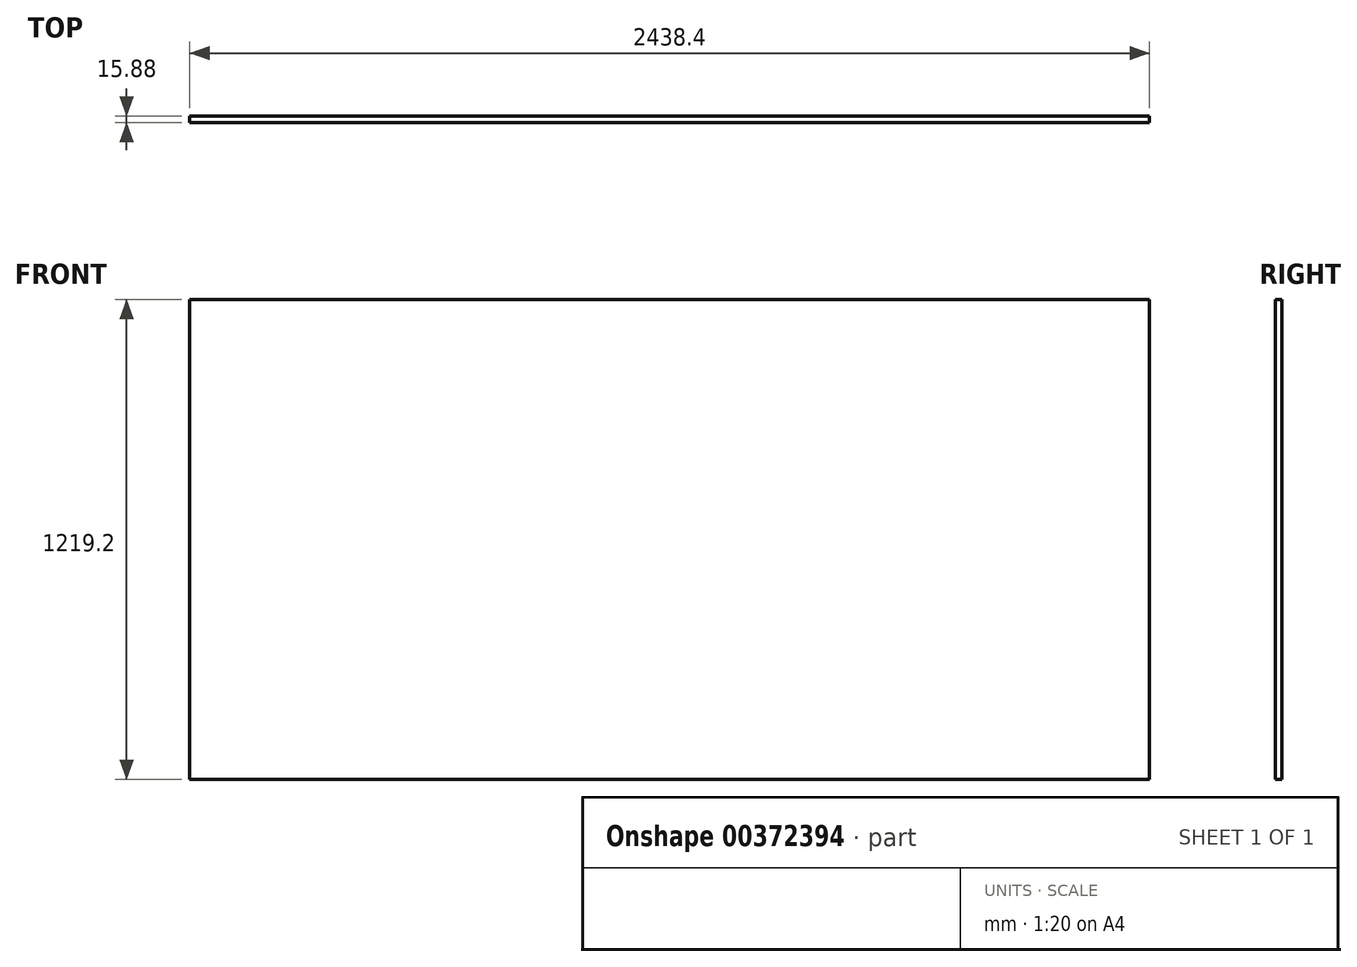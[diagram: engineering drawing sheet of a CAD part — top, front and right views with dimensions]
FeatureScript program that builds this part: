
annotation { "Feature Type Name" : "Feature", "Feature Type Description" : "" }
export const myFeature = defineFeature(function(context is Context, id is Id, definition is map)
    precondition{}
    {
        {
            var Q0;
            Q0=qCreatedBy(makeId("Front.planeOp"),FACE);
            var sketch = newSketch(context, id + "F0", { "sketchPlane" : qUnion([Q0])});
            skLineSegment(sketch, "E0.bottom", {"start": v(1219.2, -609.6) * mm, "end": v(-1219.2, -609.6) * mm});
            skLineSegment(sketch, "E0.top", {"start": v(1219.2, 609.6) * mm, "end": v(-1219.2, 609.6) * mm});
            skLineSegment(sketch, "E0.left", {"start": v(1219.2, -609.6) * mm, "end": v(1219.2, 609.6) * mm});
            skLineSegment(sketch, "E0.right", {"start": v(-1219.2, -609.6) * mm, "end": v(-1219.2, 609.6) * mm});
            skPoint(sketch, "E0.middle", {"position": v(0, 0) * mm});
            skSolve(sketch);
        }
        {
            var Q0;
            Q0=qSketchRegion(id+"F0",true);
            extrude(context, id + "F1", {"entities" : qUnion([Q0]), "depth" : 15.88 * mm});
        }
    });
